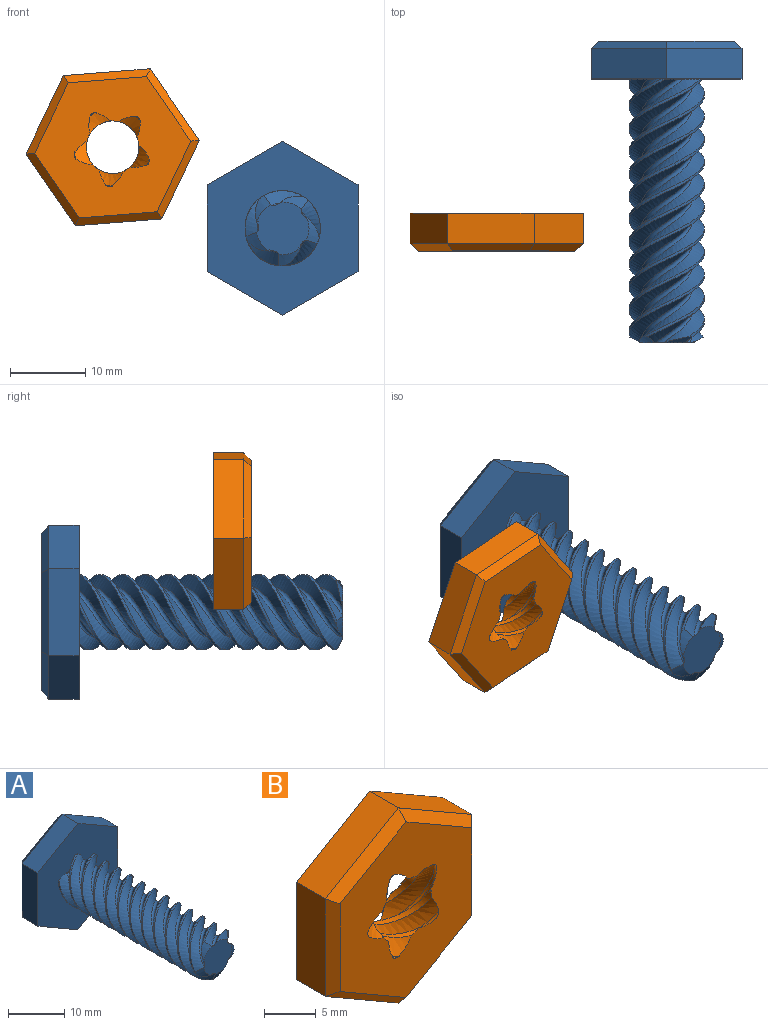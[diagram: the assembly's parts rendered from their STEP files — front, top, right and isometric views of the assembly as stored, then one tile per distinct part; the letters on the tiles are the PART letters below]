
ASSEMBLY  parts=2 mates=1
PART A: 40 faces, bbox 20.1x42x23.2 mm
  f0: cylinder r=5mm len=34.25mm, axis (0,1,0), area 28.2mm2, adj f11,f18,f28,f29
  f1: cylinder r=5mm len=34.25mm, axis (0,1,0), area 28.2mm2, adj f11,f25,f27,f30
  f2: cylinder r=5mm len=34.25mm, axis (0,1,0), area 28.2mm2, adj f11,f15,f22,f32
  f3: cylinder r=5mm len=34.25mm, axis (0,1,0), area 28.2mm2, adj f11,f19,f21,f33
  f4: cylinder r=5mm len=34.25mm, axis (0,1,0), area 28.2mm2, adj f11,f16,f24,f31
  f5: plane 11.55x4mm, normal (-1,0,0), area 46.2mm2, adj f6,f10,f11,f38
  f6: plane 10x5.77mm, normal (-0.5,0,-0.87), area 46.2mm2, adj f5,f7,f11,f39
  f7: plane 10x5.77mm, normal (0.5,0,-0.87), area 46.2mm2, adj f6,f8,f11,f37
  f8: plane 11.55x4mm, normal (1,0,0), area 46.2mm2, adj f7,f9,f11,f35
  f9: plane 10x5.77mm, normal (0.5,0,0.87), area 46.2mm2, adj f8,f10,f11,f34
  f10: plane 10x5.77mm, normal (-0.5,0,0.87), area 46.2mm2, adj f5,f9,f11,f36
  f11: plane 23.2x20.11mm, normal (0,-1,0), area 293.3mm2, adj f0,f1,f2,f3,f4,f5,f6,f7
  f12: plane 20.78x18mm, normal (0,1,0), area 280.6mm2, adj f34,f35,f36,f37,f38,f39
  f13: plane 7.08x7.03mm, normal (0,-1,0), area 37.2mm2, adj f14,f15,f16,f17,f18,f19,f20,f21
  f14: bspline ~38.25x6.75mm, area 42.3mm2, adj f11,f13,f15,f16
  f15: bspline ~38.44x10mm, area 127.2mm2, adj f2,f11,f13,f14,f32
  f16: bspline ~38.44x10mm, area 127.1mm2, adj f4,f11,f13,f14,f31
  f17: bspline ~38.25x7.11mm, area 42.3mm2, adj f11,f13,f18,f19
  f18: bspline ~38.44x10.53mm, area 127.2mm2, adj f0,f11,f13,f17,f29
  f19: bspline ~38.44x10.53mm, area 127.1mm2, adj f3,f11,f13,f17,f33
  f20: bspline ~38.25x7.29mm, area 42.3mm2, adj f11,f13,f21,f22
  f21: bspline ~38.44x10.79mm, area 127.2mm2, adj f3,f11,f13,f20,f33
  f22: bspline ~38.44x10.79mm, area 127.1mm2, adj f2,f11,f13,f20,f32
  f23: bspline ~38.25x7.29mm, area 42.3mm2, adj f11,f13,f24,f25
  f24: bspline ~38.44x10.79mm, area 127.2mm2, adj f4,f11,f13,f23,f31
  f25: bspline ~38.44x10.79mm, area 127.1mm2, adj f1,f11,f13,f23,f30
  f26: bspline ~38.25x7.11mm, area 42.3mm2, adj f11,f13,f27,f28
  f27: bspline ~38.44x10.53mm, area 127.2mm2, adj f1,f11,f13,f26,f30
  f28: bspline ~38.44x10.53mm, area 127.1mm2, adj f0,f11,f13,f26,f29
  f29: cone r=5mm half-angle=63.4deg, axis (0,1,0), area 3.5mm2, adj f0,f13,f18,f28
  f30: cone r=5mm half-angle=63.4deg, axis (0,1,0), area 3.5mm2, adj f1,f13,f25,f27
  f31: cone r=5mm half-angle=63.4deg, axis (0,1,0), area 3.5mm2, adj f4,f13,f16,f24
  f32: cone r=5mm half-angle=63.4deg, axis (0,1,0), area 3.5mm2, adj f2,f13,f15,f22
  f33: cone r=5mm half-angle=63.4deg, axis (0,1,0), area 3.5mm2, adj f3,f13,f19,f21
  f34: plane 10x6.35mm, normal (0.35,0.71,0.61), area 15.5mm2, adj f9,f12,f35,f36
  f35: plane 11.55x1mm, normal (0.71,0.71,0), area 15.5mm2, adj f8,f12,f34,f37
  f36: plane 10x6.35mm, normal (-0.35,0.71,0.61), area 15.5mm2, adj f10,f12,f34,f38
  f37: plane 10x6.35mm, normal (0.35,0.71,-0.61), area 15.5mm2, adj f7,f12,f35,f39
  f38: plane 11.55x1mm, normal (-0.71,0.71,0), area 15.5mm2, adj f5,f12,f36,f39
  f39: plane 10x6.35mm, normal (-0.35,0.71,-0.61), area 15.5mm2, adj f6,f12,f37,f38
PART B: 34 faces, bbox 20.1x9.8x23.2 mm
  f0: plane 11.55x4mm, normal (-1,0,0), area 46.2mm2, adj f1,f5,f7,f33
  f1: plane 10x5.77mm, normal (-0.5,0,-0.87), area 46.2mm2, adj f0,f2,f7,f31
  f2: plane 10x5.77mm, normal (0.5,0,-0.87), area 46.2mm2, adj f1,f3,f7,f29
  f3: plane 11.55x4mm, normal (1,0,0), area 46.2mm2, adj f2,f4,f7,f28
  f4: plane 10x5.77mm, normal (0.5,0,0.87), area 46.2mm2, adj f3,f5,f7,f30
  f5: plane 10x5.77mm, normal (-0.5,0,0.87), area 46.2mm2, adj f0,f4,f7,f32
  f6: plane 20.92x18.13mm, normal (0,-1,0), area 223.5mm2, adj f8,f9,f10,f11,f12,f13,f14,f15
  f7: plane 23.21x20.12mm, normal (0,1,0), area 289.3mm2, adj f0,f1,f2,f3,f4,f5,f8,f9
  f8: bspline ~10.78x9.69mm, area 18.8mm2, adj f6,f7,f10,f23
  f9: bspline ~10.17x7.94mm, area 18.8mm2, adj f6,f7,f10,f24
  f10: bspline ~10.45x7.38mm, area 4.8mm2, adj f6,f7,f8,f9
  f11: bspline ~9.92x9.92mm, area 18.8mm2, adj f6,f7,f13,f27
  f12: bspline ~9.92x7.94mm, area 18.8mm2, adj f6,f7,f13,f26
  f13: bspline ~10.18x7.38mm, area 4.8mm2, adj f6,f7,f11,f12
  f14: bspline ~10.14x9.69mm, area 18.8mm2, adj f6,f7,f16,f24
  f15: bspline ~10.14x7.94mm, area 18.8mm2, adj f6,f7,f16,f27
  f16: bspline ~10.41x7.38mm, area 4.8mm2, adj f6,f7,f14,f15
  f17: bspline ~10.78x9.69mm, area 18.8mm2, adj f6,f7,f19,f25
  f18: bspline ~9.63x7.94mm, area 18.8mm2, adj f6,f7,f19,f23
  f19: bspline ~9.88x7.7mm, area 4.8mm2, adj f6,f7,f17,f18
  f20: bspline ~10.14x9.69mm, area 18.8mm2, adj f6,f7,f22,f26
  f21: bspline ~8.73x8.14mm, area 18.8mm2, adj f6,f7,f22,f25
  f22: bspline ~8.96x8.35mm, area 4.8mm2, adj f6,f7,f20,f21
  f23: cylinder r=3.5mm len=5.55mm, axis (0,-1,0), area 5.5mm2, adj f6,f7,f8,f18
  f24: cylinder r=3.5mm len=5.25mm, axis (0,-1,0), area 5.5mm2, adj f6,f7,f9,f14
  f25: cylinder r=3.5mm len=6.31mm, axis (0,-1,0), area 5.5mm2, adj f6,f7,f17,f21
  f26: cylinder r=3.5mm len=6.53mm, axis (0,-1,0), area 5.5mm2, adj f6,f7,f12,f20
  f27: cylinder r=3.5mm len=6.1mm, axis (0,-1,0), area 5.5mm2, adj f6,f7,f11,f15
  f28: plane 11.55x1mm, normal (0.71,-0.71,0), area 15.5mm2, adj f3,f6,f29,f30
  f29: plane 10x6.35mm, normal (0.35,-0.71,-0.61), area 15.5mm2, adj f2,f6,f28,f31
  f30: plane 10x6.35mm, normal (0.35,-0.71,0.61), area 15.5mm2, adj f4,f6,f28,f32
  f31: plane 10x6.35mm, normal (-0.35,-0.71,-0.61), area 15.5mm2, adj f1,f6,f29,f33
  f32: plane 10x6.35mm, normal (-0.35,-0.71,0.61), area 15.5mm2, adj f5,f6,f30,f33
  f33: plane 11.55x1mm, normal (-0.71,-0.71,0), area 15.5mm2, adj f0,f6,f31,f32
PLACE A t=(2.93,-9.71,3.81)mm fixed
PLACE B rot(axis=(0,-1,0),154.5deg) t=(2.93,-32.57,3.81)mm
MATE cylindrical A.f0 <-> B.f6  axis (0,1,0) through (2.93,-9.71,3.81)mm
